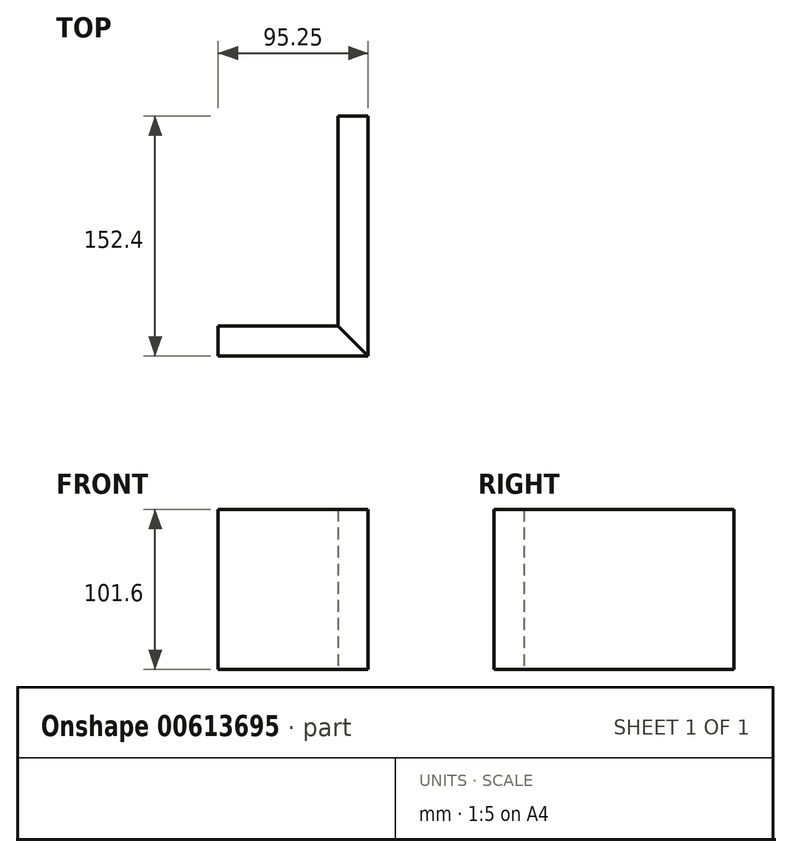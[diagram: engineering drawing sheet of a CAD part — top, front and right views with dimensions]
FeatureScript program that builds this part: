
annotation { "Feature Type Name" : "Feature", "Feature Type Description" : "" }
export const myFeature = defineFeature(function(context is Context, id is Id, definition is map)
    precondition{}
    {
        {
            var Q0;
            Q0=qCreatedBy(makeId("Top.planeOp"),FACE);
            var sketch = newSketch(context, id + "F0", { "sketchPlane" : qUnion([Q0])});
            skLineSegment(sketch, "E0.bottom", {"start": v(0, 0) * mm, "end": v(-76.2, 0) * mm});
            skLineSegment(sketch, "E0.top", {"start": v(0, 19.05) * mm, "end": v(-76.2, 19.05) * mm});
            skLineSegment(sketch, "E0.left", {"start": v(0, 0) * mm, "end": v(0, 19.05) * mm});
            skLineSegment(sketch, "E0.right", {"start": v(-76.2, 0) * mm, "end": v(-76.2, 19.05) * mm});
            skLineSegment(sketch, "E1.bottom", {"start": v(0, 0) * mm, "end": v(19.05, 0) * mm});
            skLineSegment(sketch, "E1.top", {"start": v(0, 152.4) * mm, "end": v(19.05, 152.4) * mm});
            skLineSegment(sketch, "E1.left", {"start": v(0, 0) * mm, "end": v(0, 152.4) * mm});
            skLineSegment(sketch, "E1.right", {"start": v(19.05, 0) * mm, "end": v(19.05, 152.4) * mm});
            skLineSegment(sketch, "E2", {"start": v(0, 19.05) * mm, "end": v(19.05, 0) * mm});
            skSolve(sketch);
        }
        {
            var Q0;
            {var subQ0=sQuery(id+"F0.wireOp",EDGE,"E1.top");Q0=makeQuery(id+"F0.imprint","IMPRINT",FACE,{"disambiguationData":[TD([[makeQuery(id+"F0.imprint","IMPRINT",EDGE,{"derivedFrom":subQ0}),-1.0]])]});}
            extrude(context, id + "F1", {"entities" : qUnion([Q0]), "depth" : 101.6 * mm, "offsetDistance" : 25.4 * mm});
        }
        {
            var Q0;
            Q0 = qSketchRegion(id + "F0", true);
            extrude(context, id + "F2", {"entities" : qUnion([Q0]), "depth" : 101.6 * mm, "offsetDistance" : 25.4 * mm});
        }
    });
